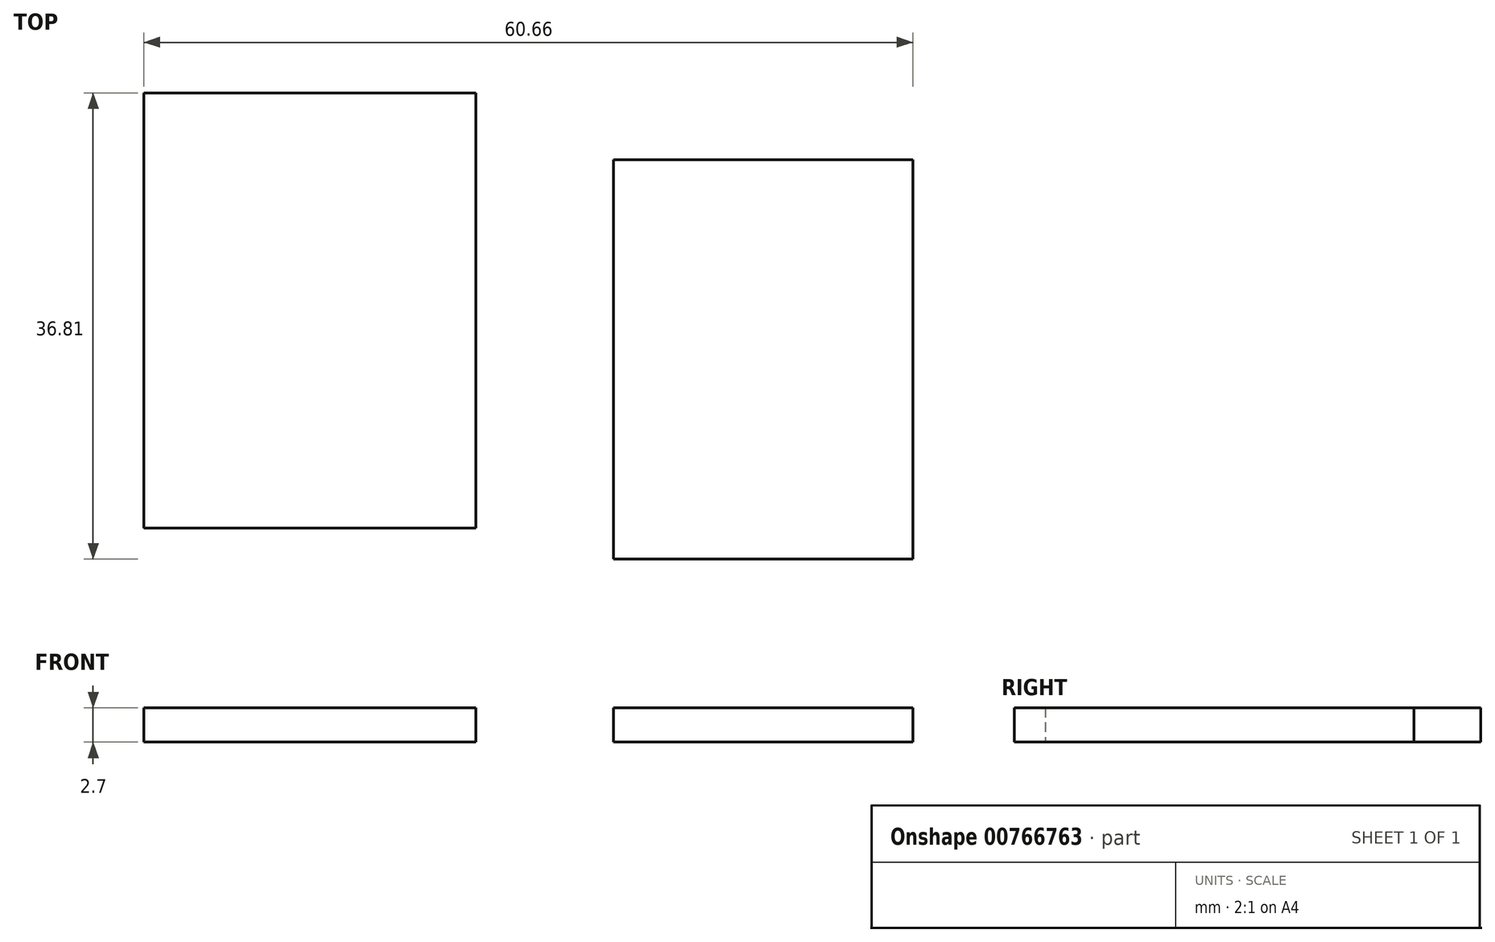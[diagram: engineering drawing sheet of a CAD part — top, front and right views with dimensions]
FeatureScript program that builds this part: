
annotation { "Feature Type Name" : "Feature", "Feature Type Description" : "" }
export const myFeature = defineFeature(function(context is Context, id is Id, definition is map)
    precondition{}
    {
        {
            var Q0;
            Q0=qCreatedBy(makeId("Top.planeOp"),FACE);
            var sketch = newSketch(context, id + "F0", { "sketchPlane" : qUnion([Q0])});
            skLineSegment(sketch, "E0.bottom", {"start": v(-133.34, 41.78) * mm, "end": v(-107.14, 41.78) * mm});
            skLineSegment(sketch, "E0.top", {"start": v(-133.34, 7.42) * mm, "end": v(-107.14, 7.42) * mm});
            skLineSegment(sketch, "E0.left", {"start": v(-133.34, 41.78) * mm, "end": v(-133.34, 7.42) * mm});
            skLineSegment(sketch, "E0.right", {"start": v(-107.14, 41.78) * mm, "end": v(-107.14, 7.42) * mm});
            skLineSegment(sketch, "E1.bottom", {"start": v(-96.3, 4.97) * mm, "end": v(-72.68, 4.97) * mm});
            skLineSegment(sketch, "E1.top", {"start": v(-96.3, 36.5) * mm, "end": v(-72.68, 36.5) * mm});
            skLineSegment(sketch, "E1.left", {"start": v(-96.3, 4.97) * mm, "end": v(-96.3, 36.5) * mm});
            skLineSegment(sketch, "E1.right", {"start": v(-72.68, 4.97) * mm, "end": v(-72.68, 36.5) * mm});
            skSolve(sketch);
        }
        {
            var Q0;
            Q0 = qSketchRegion(id + "F0", true);
            extrude(context, id + "F1", {"entities" : qUnion([Q0]), "depth" : 2.7 * mm, "offsetDistance" : 25 * mm});
        }
    });
